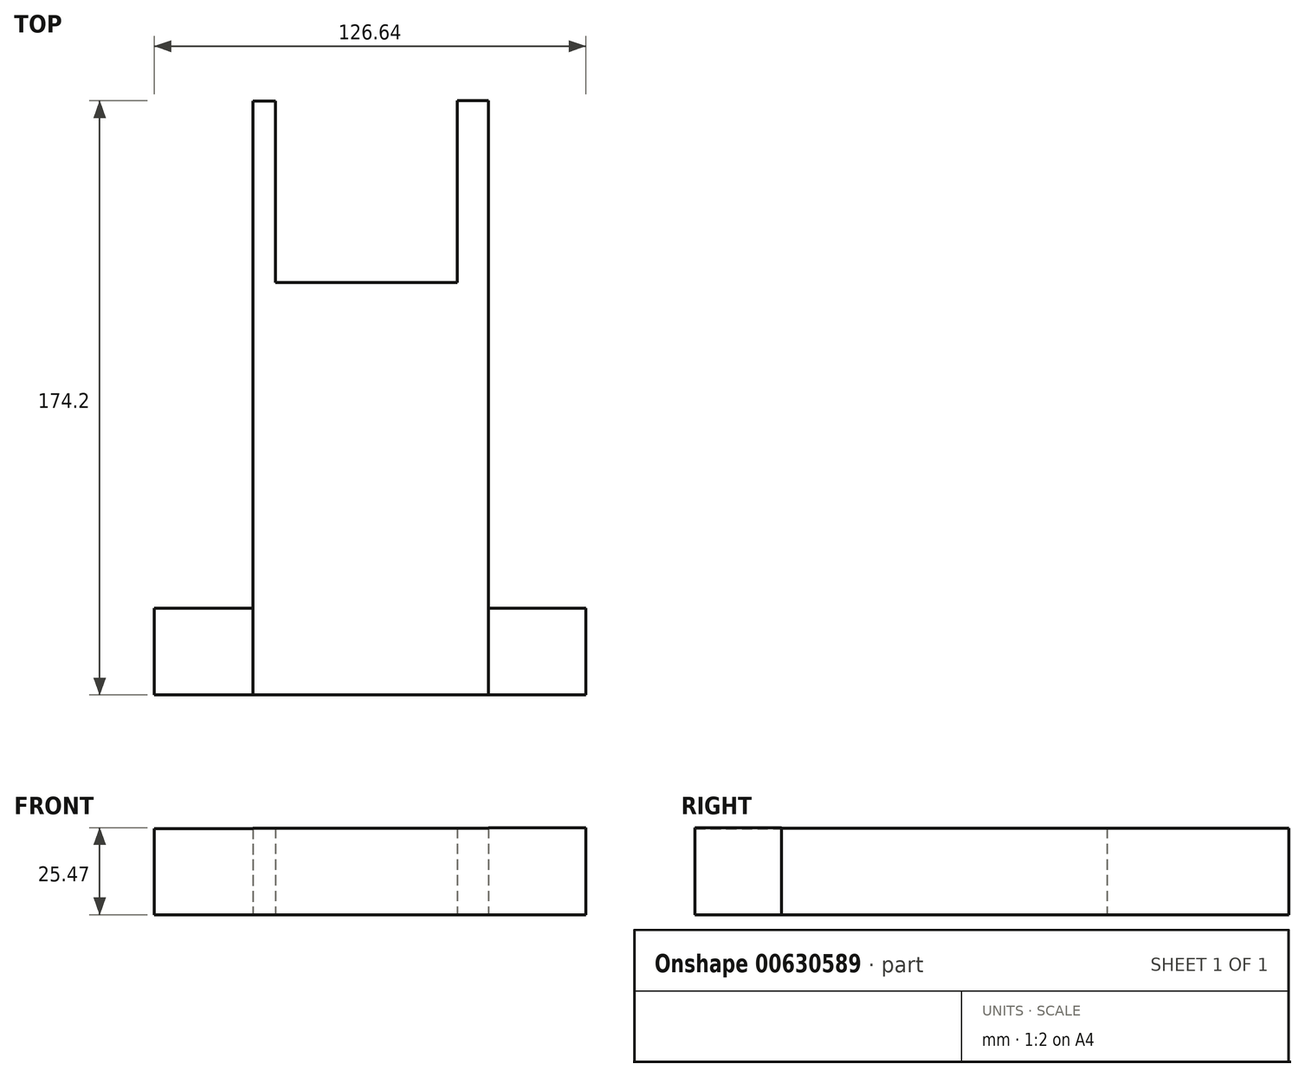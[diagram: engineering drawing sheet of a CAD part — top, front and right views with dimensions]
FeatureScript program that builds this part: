
annotation { "Feature Type Name" : "Feature", "Feature Type Description" : "" }
export const myFeature = defineFeature(function(context is Context, id is Id, definition is map)
    precondition{}
    {
        {
            var Q0;
            Q0=qCreatedBy(makeId("Top.planeOp"),FACE);
            var sketch = newSketch(context, id + "F0", { "sketchPlane" : qUnion([Q0])});
            skLineSegment(sketch, "E0.bottom", {"start": v(-34.4, 47.63) * mm, "end": v(34.68, 47.63) * mm});
            skLineSegment(sketch, "E0.top", {"start": v(-34.4, -47.92) * mm, "end": v(34.68, -47.92) * mm});
            skLineSegment(sketch, "E0.left", {"start": v(-34.4, 47.63) * mm, "end": v(-34.4, -47.92) * mm});
            skLineSegment(sketch, "E0.right", {"start": v(34.68, 47.63) * mm, "end": v(34.68, -47.92) * mm});
            skSolve(sketch);
        }
        {
            var Q0;
            Q0=makeQuery(id+"F0.imprint","IMPRINT",FACE,{"disambiguationData":[TD([[makeQuery(id+"F0.imprint","IMPRINT",EDGE,{"derivedFrom":sQuery(id+"F0.wireOp",EDGE,"E0.bottom")}),-1.0]])]});
            extrude(context, id + "F1", {"entities" : qUnion([Q0]), "depth" : 25.4 * mm, "offsetDistance" : 25.4 * mm});
        }
        {
            var Q0;
            Q0=makeQuery(id+"F1.opExtrude","SWEPT_FACE",FACE,{"disambiguationData":[OSD([sQuery(id+"F0.wireOp",EDGE,"E0.top")])]});
            var sketch = newSketch(context, id + "F2", { "sketchPlane" : qUnion([Q0])});
            skLineSegment(sketch, "E1.bottom", {"start": v(34.68, 0) * mm, "end": v(63.28, 0) * mm});
            skLineSegment(sketch, "E1.top", {"start": v(34.68, 25.47) * mm, "end": v(63.28, 25.47) * mm});
            skLineSegment(sketch, "E1.left", {"start": v(34.68, 0) * mm, "end": v(34.68, 25.47) * mm});
            skLineSegment(sketch, "E1.right", {"start": v(63.28, 0) * mm, "end": v(63.28, 25.47) * mm});
            skLineSegment(sketch, "E2.bottom", {"start": v(-34.4, 0) * mm, "end": v(-63.36, 0) * mm});
            skLineSegment(sketch, "E2.top", {"start": v(-34.4, 25.2) * mm, "end": v(-63.36, 25.2) * mm});
            skLineSegment(sketch, "E2.left", {"start": v(-34.4, 0) * mm, "end": v(-34.4, 25.2) * mm});
            skLineSegment(sketch, "E2.right", {"start": v(-63.36, 0) * mm, "end": v(-63.36, 25.2) * mm});
            skSolve(sketch);
        }
        {
            var Q0;
            Q0 = qSketchRegion(id + "F2", true);
            var Q1;
            {var subQ4=sQuery(id+"F2.wireOp",EDGE,"E2.left");Q1=makeQuery(id+"F2.imprint","IMPRINT",FACE,{"disambiguationData":[TD([[makeQuery(id+"F2.imprint","IMPRINT",EDGE,{"derivedFrom":subQ4}),1.0]])]});}
            extrude(context, id + "F3", {"entities" : qUnion([Q0, Q1]), "operationType" : NewBodyOperationType.ADD, "depth" : 25.4 * mm, "offsetDistance" : 25.4 * mm});
        }
        {
            var Q0;
            Q0=makeQuery(id+"F1.opExtrude","SWEPT_FACE",FACE,{"disambiguationData":[OSD([sQuery(id+"F0.wireOp",EDGE,"E0.right")])]});
            var sketch = newSketch(context, id + "F4", { "sketchPlane" : qUnion([Q0])});
            skLineSegment(sketch, "E3", {"start": v(47.63, 25.4) * mm, "end": v(100.88, 25.4) * mm});
            skLineSegment(sketch, "E4", {"start": v(100.88, 25.4) * mm, "end": v(100.88, 0) * mm});
            skLineSegment(sketch, "E5", {"start": v(100.88, 0) * mm, "end": v(47.63, 0) * mm});
            skSolve(sketch);
        }
        {
            var Q0;
            Q0 = qSketchRegion(id + "F4", true);
            var Q1;
            Q1=makeQuery(id+"F4.imprint","IMPRINT",FACE,{"disambiguationData":[TD([[makeQuery(id+"F4.imprint","IMPRINT",EDGE,{"derivedFrom":sQuery(id+"F4.wireOp",EDGE,"E3")}),-1.0]])]});
            extrude(context, id + "F5", {"entities" : qUnion([Q0, Q1]), "operationType" : NewBodyOperationType.ADD, "oppositeDirection" : true, "depth" : 9.14 * mm, "offsetDistance" : 25.4 * mm});
        }
        {
            var Q0;
            {var subQ0=sQuery(id+"F0.wireOp",EDGE,"E0.left");Q0=makeQuery(id+"F3.boolean.opBoolean","MERGE",FACE,{"derivedFrom":[makeQuery(id+"F1.opExtrude","SWEPT_FACE",FACE,{"disambiguationData":[OSD([subQ0])]}),makeQuery(id+"F3.opExtrude","SWEPT_FACE",FACE,{"disambiguationData":[OSD([sQuery(id+"F0.wireOp",EDGE,"E0.top"),subQ0])]})]});}
            var sketch = newSketch(context, id + "F6", { "sketchPlane" : qUnion([Q0])});
            skLineSegment(sketch, "E6", {"start": v(-47.63, 25.4) * mm, "end": v(-100.84, 25.4) * mm});
            skLineSegment(sketch, "E7", {"start": v(-100.84, 25.4) * mm, "end": v(-100.84, 0) * mm});
            skLineSegment(sketch, "E8", {"start": v(-100.84, 0) * mm, "end": v(-47.63, 0) * mm});
            skSolve(sketch);
        }
        {
            var Q0;
            Q0 = qSketchRegion(id + "F6", true);
            var Q1;
            Q1=makeQuery(id+"F6.imprint","IMPRINT",FACE,{"disambiguationData":[TD([[makeQuery(id+"F6.imprint","IMPRINT",EDGE,{"derivedFrom":sQuery(id+"F6.wireOp",EDGE,"E6")}),1.0]])]});
            extrude(context, id + "F7", {"entities" : qUnion([Q0, Q1]), "operationType" : NewBodyOperationType.ADD, "oppositeDirection" : true, "depth" : 6.6 * mm, "offsetDistance" : 25.4 * mm});
        }
    });
